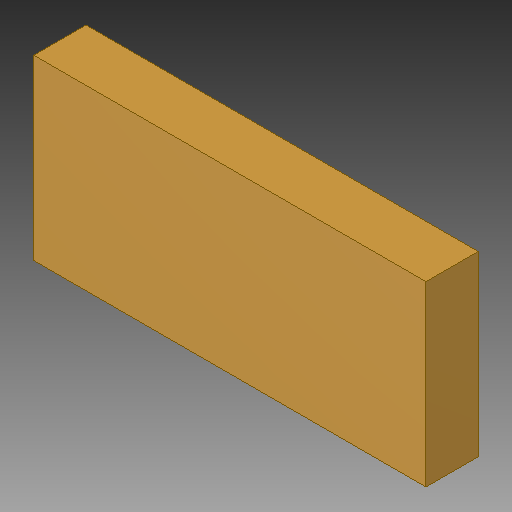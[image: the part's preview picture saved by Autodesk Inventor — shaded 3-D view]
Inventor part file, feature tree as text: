
AUTODESK INVENTOR PART (.ipt)
format: ipt  version: 2019 (Build 230136000, 136)  size: 89,088 bytes
history: native  units: in
note: dims shown in document units (in); Inventor stores cm internally (conversion verified against a paired STEP export)
features: extrude x1, other x1
ambient origin geometry x8: Origin, YZ Plane, XZ Plane, XY Plane, X Axis, Y Axis, Z Axis, Center Point
bodies: Solid1 (feature_tree)
feature tree (2):
  extrude  "Extrusion1"  Depth=0.0394in TaperAngle=0.0deg
  other  "B4B-ZR, B4B-ZR_6"
